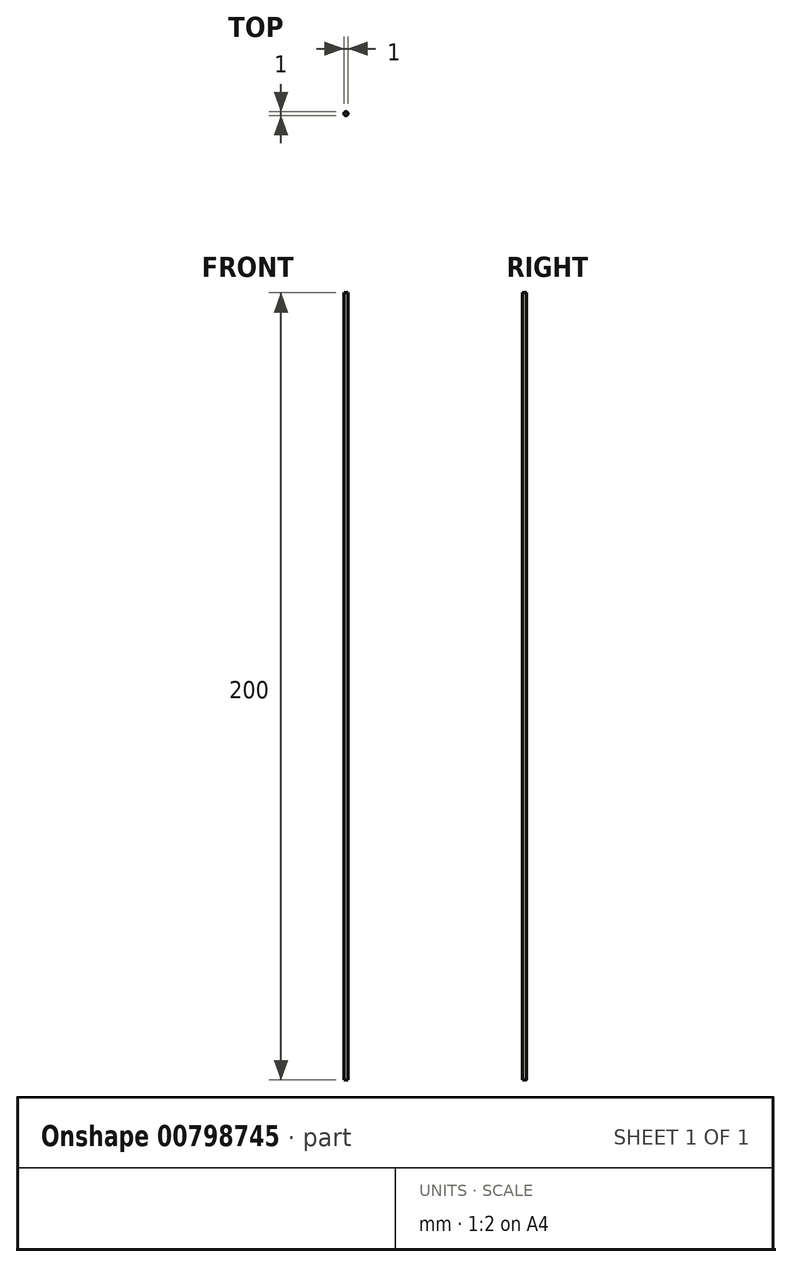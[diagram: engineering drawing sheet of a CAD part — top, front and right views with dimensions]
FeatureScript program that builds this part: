
annotation { "Feature Type Name" : "Feature", "Feature Type Description" : "" }
export const myFeature = defineFeature(function(context is Context, id is Id, definition is map)
    precondition{}
    {
        {
            var Q0;
            Q0=qCreatedBy(makeId("Top.planeOp"),FACE);
            var sketch = newSketch(context, id + "F0", { "sketchPlane" : qUnion([Q0])});
            skCircle(sketch, "E0", {"center": v(0, 100) * mm, "radius": 0.5 * mm});
            skSolve(sketch);
        }
        {
            var Q0;
            Q0=qSketchRegion(id+"F0",true);
            extrude(context, id + "F1", {"entities" : qUnion([Q0]), "depth" : 200 * mm, "offsetDistance" : 25 * mm});
        }
        {
            var Q0;
            Q0=qCreatedBy(makeId("Right.planeOp"),FACE);
            var sketch = newSketch(context, id + "F2", { "sketchPlane" : qUnion([Q0])});
            skLineSegment(sketch, "E1", {"start": v(0, 0) * mm, "end": v(0, 43.15) * mm});
            skSolve(sketch);
        }
    });
